# Revit family: Sink-Vessel-Lavatory-KOHLER-BENJARONG_KARESS-K-98420T_1
name_source: partatom
category: Plumbing Fixtures
revit_build: Autodesk Revit 2017 (Build: 20160225_1515(x64)
units: mm (PartAtom-declared; Revit-internal decimal feet)

## family parameters
Cut with Voids When Loaded = No
Host = Face
OmniClass Number = 23.31.13.00
OmniClass Title = Sinks
Part Type = Normal
Room Calculation Point = No
Round Connector Dimension = Use Diameter
Shared = No

## types (2) — shared parameters
ADA Compliant = No
Assembly Code = D2010400
CW Connection = No
Cold Water Inlet = Cold Water Inlet
Date Modified = 08/10/2021
Default Elevation = 36"
Drain Included = No
Finish = Kohler-Vitreous_China-0-White
HW Connection = No
Height = 7 13/16"
Hot Water Inlet = Hot Water Inlet
Length = 17 7/16"
Manufacturer = KOHLER Co.
Master Format 2014 = 22 41 16
Master Format 2014 Name = Residential Lavatories and Sinks
Material = Vitreous China
Product Name = BENJARONG KARESS
Product Page URL = https://www.kohler.com.cn
URL = http://www.kohler.com.cn
Vent Connection = No
Waste Connection = Yes
Waste Water Outlet = Waste Water Outlet
WaterSense Certified = No
Width = 24 3/16"

## per-type parameters (varying)
| type | Description | Drain Finish | Model | Type |
| Gold, 0-White | Colorful Xingluo Art Bowl | Kohler-Metal-Gold | K-98420T-TG-0 | 1 |
| Platinum, 0-White | Silver Color Xingluo Art Washbasin | Kohler-Metal-Platinum | K-98420T-TS-0 | 2 |

## geometry (parser evidence)
native form markers: Sweep x3
no freeform markers — native parametric forms only
